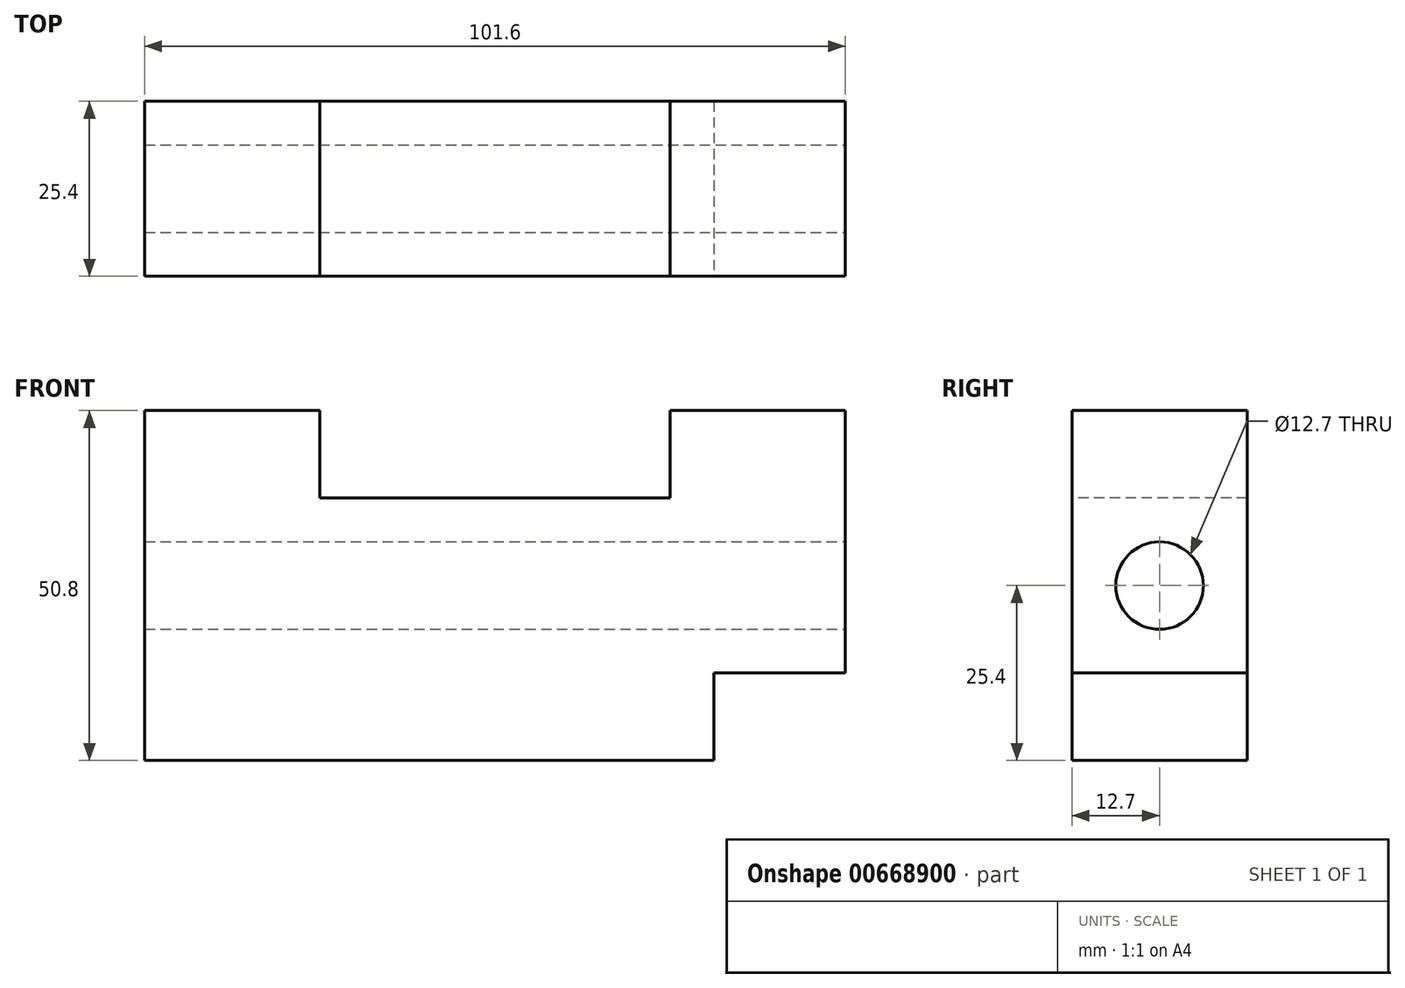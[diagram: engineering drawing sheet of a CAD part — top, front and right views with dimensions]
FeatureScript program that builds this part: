
annotation { "Feature Type Name" : "Feature", "Feature Type Description" : "" }
export const myFeature = defineFeature(function(context is Context, id is Id, definition is map)
    precondition{}
    {
        {
            var Q0;
            Q0=qCreatedBy(makeId("Front.planeOp"),FACE);
            var sketch = newSketch(context, id + "F0", { "sketchPlane" : qUnion([Q0])});
            skLineSegment(sketch, "E0.bottom", {"start": v(-50.8, 25.4) * mm, "end": v(50.8, 25.4) * mm});
            skLineSegment(sketch, "E0.top", {"start": v(-50.8, -25.4) * mm, "end": v(50.8, -25.4) * mm});
            skLineSegment(sketch, "E0.left", {"start": v(-50.8, 25.4) * mm, "end": v(-50.8, -25.4) * mm});
            skLineSegment(sketch, "E0.right", {"start": v(50.8, 25.4) * mm, "end": v(50.8, -25.4) * mm});
            skPoint(sketch, "E0.middle", {"position": v(0, 0) * mm});
            skSolve(sketch);
        }
        {
            var Q0;
            Q0 = qSketchRegion(id + "F0", true);
            extrude(context, id + "F1", {"entities" : qUnion([Q0]), "depth" : 25.4 * mm, "offsetDistance" : 25.4 * mm});
        }
        {
            var Q0;
            Q0=makeQuery(id+"F1.opExtrude","CAP_FACE",FACE,{"disambiguationData":[OSD([sQuery(id+"F0.wireOp",EDGE,"E0.bottom"),sQuery(id+"F0.wireOp",EDGE,"E0.top"),sQuery(id+"F0.wireOp",EDGE,"E0.left"),sQuery(id+"F0.wireOp",EDGE,"E0.right")])],"isStart":false});
            var sketch = newSketch(context, id + "F2", { "sketchPlane" : qUnion([Q0])});
            skLineSegment(sketch, "E1.bottom", {"start": v(-25.4, 25.4) * mm, "end": v(25.4, 25.4) * mm});
            skLineSegment(sketch, "E1.top", {"start": v(-25.4, 12.7) * mm, "end": v(25.4, 12.7) * mm});
            skLineSegment(sketch, "E1.left", {"start": v(-25.4, 25.4) * mm, "end": v(-25.4, 12.7) * mm});
            skLineSegment(sketch, "E1.right", {"start": v(25.4, 25.4) * mm, "end": v(25.4, 12.7) * mm});
            skSolve(sketch);
        }
        {
            var Q0;
            Q0 = qSketchRegion(id + "F2", true);
            extrude(context, id + "F3", {"entities" : qUnion([Q0]), "operationType" : NewBodyOperationType.REMOVE, "endBound" : BoundingType.THROUGH_ALL, "oppositeDirection" : true, "depth" : 25.4 * mm, "offsetDistance" : 25.4 * mm});
        }
        {
            var Q0;
            Q0=makeQuery(id+"F1.opExtrude","CAP_FACE",FACE,{"disambiguationData":[OSD([sQuery(id+"F0.wireOp",EDGE,"E0.bottom"),sQuery(id+"F0.wireOp",EDGE,"E0.top"),sQuery(id+"F0.wireOp",EDGE,"E0.left"),sQuery(id+"F0.wireOp",EDGE,"E0.right")])],"isStart":false});
            var sketch = newSketch(context, id + "F4", { "sketchPlane" : qUnion([Q0])});
            skLineSegment(sketch, "E2.bottom", {"start": v(50.8, -25.4) * mm, "end": v(31.75, -25.4) * mm});
            skLineSegment(sketch, "E2.top", {"start": v(50.8, -12.7) * mm, "end": v(31.75, -12.7) * mm});
            skLineSegment(sketch, "E2.left", {"start": v(50.8, -25.4) * mm, "end": v(50.8, -12.7) * mm});
            skLineSegment(sketch, "E2.right", {"start": v(31.75, -25.4) * mm, "end": v(31.75, -12.7) * mm});
            skSolve(sketch);
        }
        {
            var Q0;
            Q0 = qSketchRegion(id + "F4", true);
            extrude(context, id + "F5", {"entities" : qUnion([Q0]), "operationType" : NewBodyOperationType.REMOVE, "endBound" : BoundingType.THROUGH_ALL, "oppositeDirection" : true, "depth" : 25.4 * mm, "offsetDistance" : 25.4 * mm});
        }
        {
            var Q0;
            Q0=makeQuery(id+"F1.opExtrude","SWEPT_FACE",FACE,{"disambiguationData":[OSD([sQuery(id+"F0.wireOp",EDGE,"E0.right")])]});
            var sketch = newSketch(context, id + "F6", { "sketchPlane" : qUnion([Q0])});
            skCircle(sketch, "E3", {"center": v(-12.7, 0) * mm, "radius": 6.35 * mm});
            skSolve(sketch);
        }
        {
            var Q0;
            Q0 = qSketchRegion(id + "F6", true);
            extrude(context, id + "F7", {"entities" : qUnion([Q0]), "operationType" : NewBodyOperationType.REMOVE, "endBound" : BoundingType.THROUGH_ALL, "oppositeDirection" : true, "depth" : 25.4 * mm, "offsetDistance" : 25.4 * mm});
        }
    });
